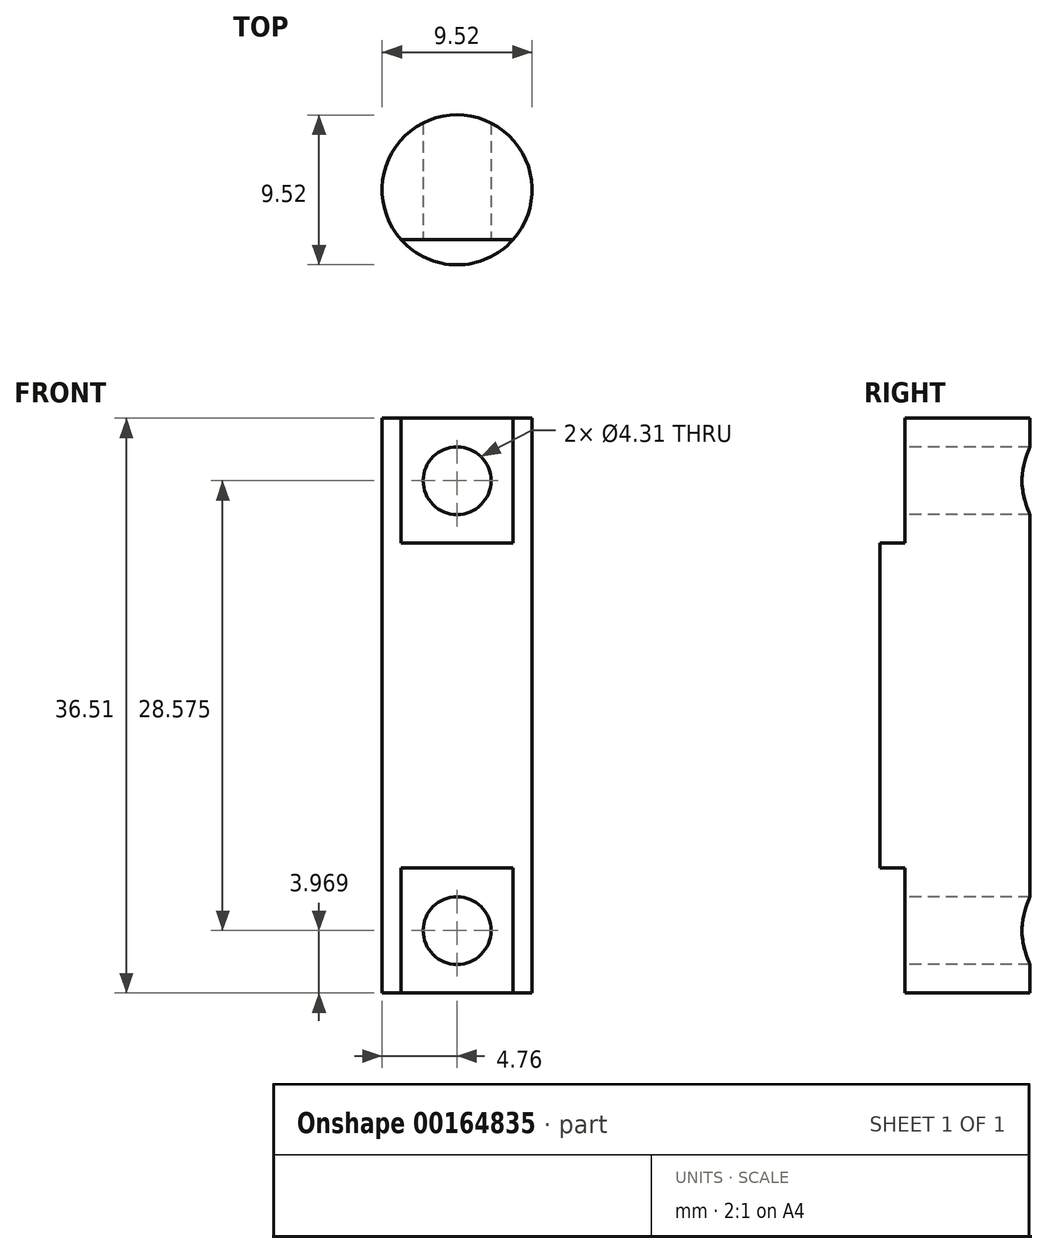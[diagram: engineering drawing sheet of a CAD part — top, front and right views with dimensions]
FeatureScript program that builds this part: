
annotation { "Feature Type Name" : "Feature", "Feature Type Description" : "" }
export const myFeature = defineFeature(function(context is Context, id is Id, definition is map)
    precondition{}
    {
        {
            var Q0;
            Q0=qCreatedBy(makeId("Top.planeOp"),FACE);
            var sketch = newSketch(context, id + "F0", { "sketchPlane" : qUnion([Q0])});
            skCircle(sketch, "E0", {"center": v(0, 0) * mm, "radius": 4.76 * mm});
            skSolve(sketch);
        }
        {
            var Q0;
            Q0 = qSketchRegion(id + "F0", true);
            extrude(context, id + "F1", {"entities" : qUnion([Q0]), "depth" : 36.5 * mm});
        }
        {
            var Q0;
            Q0=makeQuery(id+"F1.opExtrude","CAP_FACE",FACE,{"disambiguationData":[OSD([sQuery(id+"F0.wireOp",EDGE,"E0")])],"isStart":false});
            var sketch = newSketch(context, id + "F2", { "sketchPlane" : qUnion([Q0])});
            skLineSegment(sketch, "E1.bottom", {"start": v(-3.55, -3.17) * mm, "end": v(3.55, -3.17) * mm});
            skLineSegment(sketch, "E1.top", {"start": v(-3.55, -4.76) * mm, "end": v(3.55, -4.76) * mm});
            skLineSegment(sketch, "E1.left", {"start": v(-3.55, -4.76) * mm, "end": v(-3.55, -3.17) * mm});
            skLineSegment(sketch, "E1.right", {"start": v(3.55, -4.76) * mm, "end": v(3.55, -3.17) * mm});
            skSolve(sketch);
        }
        {
            var Q0;
            Q0 = qSketchRegion(id + "F2", true);
            extrude(context, id + "F3", {"entities" : qUnion([Q0]), "operationType" : NewBodyOperationType.REMOVE, "oppositeDirection" : true, "depth" : 7.94 * mm});
        }
        {
            var Q0;
            Q0=makeQuery(id+"F1.opExtrude","CAP_FACE",FACE,{"disambiguationData":[OSD([sQuery(id+"F0.wireOp",EDGE,"E0")])],"isStart":true});
            var sketch = newSketch(context, id + "F4", { "sketchPlane" : qUnion([Q0])});
            skLineSegment(sketch, "E2.bottom", {"start": v(-3.55, 3.17) * mm, "end": v(3.55, 3.17) * mm});
            skLineSegment(sketch, "E2.top", {"start": v(-3.55, 4.76) * mm, "end": v(3.55, 4.76) * mm});
            skLineSegment(sketch, "E2.left", {"start": v(-3.55, 3.17) * mm, "end": v(-3.55, 4.76) * mm});
            skLineSegment(sketch, "E2.right", {"start": v(3.55, 3.17) * mm, "end": v(3.55, 4.76) * mm});
            skSolve(sketch);
        }
        {
            var Q0;
            Q0 = qSketchRegion(id + "F4", true);
            extrude(context, id + "F5", {"entities" : qUnion([Q0]), "operationType" : NewBodyOperationType.REMOVE, "oppositeDirection" : true, "depth" : 7.94 * mm});
        }
        {
            var Q0;
            Q0=makeQuery(id+"F5.boolean.opBoolean","COPY",FACE,{"derivedFrom":makeQuery(id+"F5.opExtrude","SWEPT_FACE",FACE,{"disambiguationData":[OSD([sQuery(id+"F4.wireOp",EDGE,"E2.bottom")])]})});
            var sketch = newSketch(context, id + "F6", { "sketchPlane" : qUnion([Q0])});
            skLineSegment(sketch, "E3", {"start": v(3.55, 32.54) * mm, "end": v(-3.55, 32.54) * mm, "construction": true});
            skCircle(sketch, "E4", {"center": v(0, 32.54) * mm, "radius": 2.15 * mm});
            skLineSegment(sketch, "E5", {"start": v(3.55, 3.97) * mm, "end": v(-3.55, 3.97) * mm, "construction": true});
            skCircle(sketch, "E6", {"center": v(0, 3.97) * mm, "radius": 2.15 * mm});
            skSolve(sketch);
        }
        {
            var Q0;
            Q0 = qSketchRegion(id + "F6", true);
            var Q1;
            Q1=makeQuery(id+"F1.opExtrude","SWEPT_FACE",FACE,{"disambiguationData":[OSD([sQuery(id+"F0.wireOp",EDGE,"E0")])]});
            extrude(context, id + "F7", {"entities" : qUnion([Q0]), "operationType" : NewBodyOperationType.REMOVE, "endBound" : BoundingType.UP_TO_SURFACE, "oppositeDirection" : true, "endBoundEntityFace" : qUnion([Q1]), "depth" : 25.4 * mm});
        }
    });
